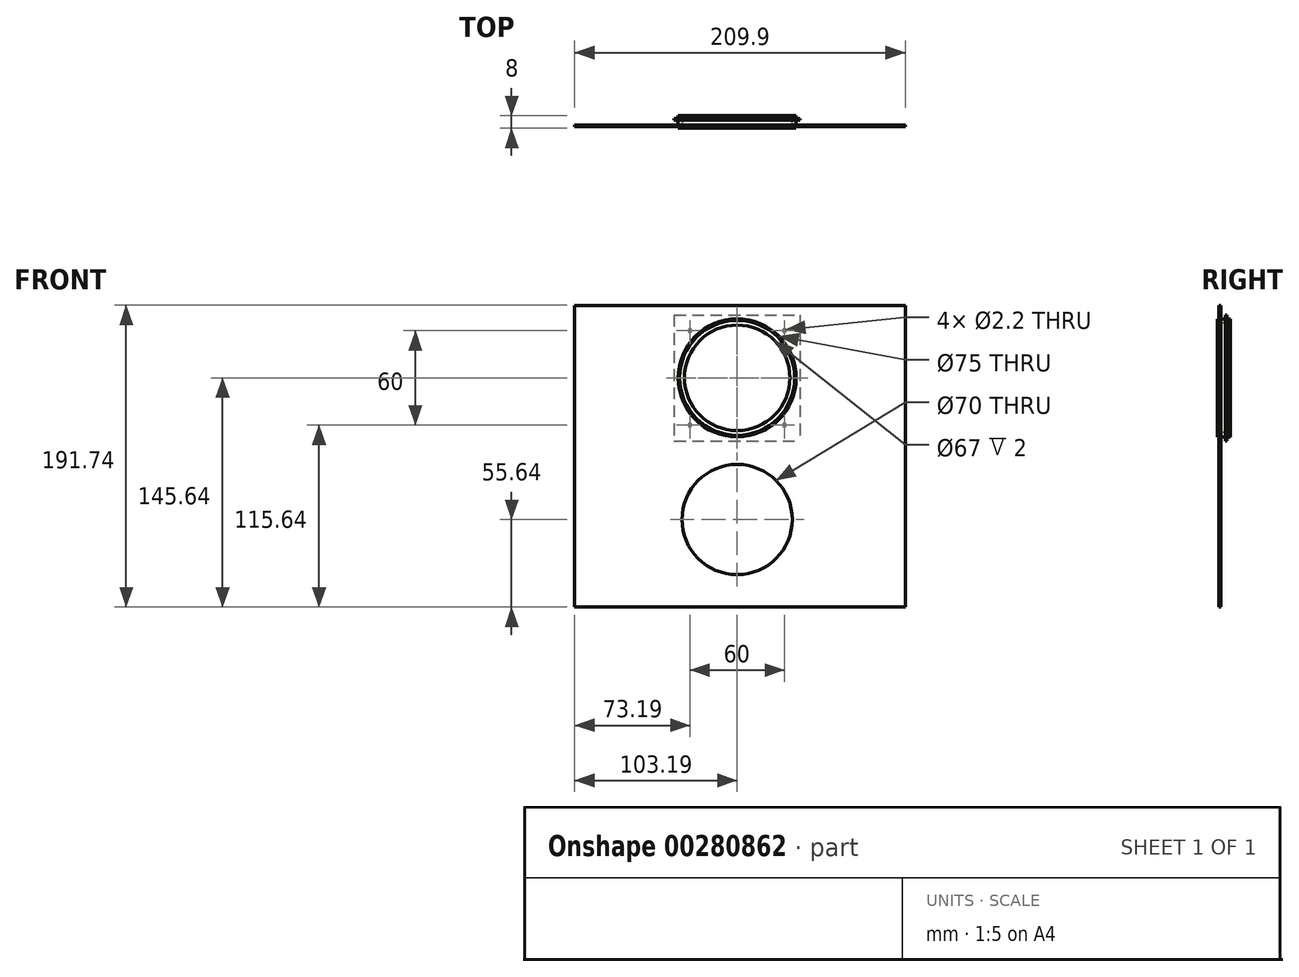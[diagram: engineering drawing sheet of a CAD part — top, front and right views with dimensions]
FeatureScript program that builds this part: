
annotation { "Feature Type Name" : "Feature", "Feature Type Description" : "" }
export const myFeature = defineFeature(function(context is Context, id is Id, definition is map)
    precondition{}
    {
        {
            var Q0;
            Q0=qCreatedBy(makeId("Front.planeOp"),FACE);
            cPlane(context, id + "F0", {"entities" : qUnion([Q0]), "cplaneType" : CPlaneType.OFFSET, "offset" : 5 * mm, "width" : 150 * mm, "height" : 150 * mm});
        }
        {
            var Q0;
            Q0=qCreatedBy(id+"F0.planeOp",FACE);
            var sketch = newSketch(context, id + "F1", { "sketchPlane" : qUnion([Q0])});
            skCircle(sketch, "E0", {"center": v(0, 0) * mm, "radius": 37.5 * mm});
            skCircle(sketch, "E1", {"center": v(0, -90) * mm, "radius": 35 * mm});
            skLineSegment(sketch, "E2.bottom", {"start": v(-103.2, 46.1) * mm, "end": v(106.7, 46.1) * mm});
            skLineSegment(sketch, "E2.top", {"start": v(-103.2, -145.64) * mm, "end": v(106.7, -145.64) * mm});
            skLineSegment(sketch, "E2.left", {"start": v(-103.2, 46.1) * mm, "end": v(-103.2, -145.64) * mm});
            skLineSegment(sketch, "E2.right", {"start": v(106.7, 46.1) * mm, "end": v(106.7, -145.64) * mm});
            skSolve(sketch);
        }
        {
            var Q0;
            Q0=qSketchRegion(id+"F1",true);
            extrude(context, id + "F2", {"entities" : qUnion([Q0]), "oppositeDirection" : true, "depth" : 1 * mm});
        }
        {
            var Q0;
            Q0=qCreatedBy(makeId("Right.planeOp"),FACE);
            var sketch = newSketch(context, id + "F3", { "sketchPlane" : qUnion([Q0])});
            skLineSegment(sketch, "E3", {"start": v(19.32, 0) * mm, "end": v(-16.11, 0) * mm, "construction": true});
            skLineSegment(sketch, "E4", {"start": v(-6, 37.5) * mm, "end": v(-6, 36.5) * mm});
            skLineSegment(sketch, "E5", {"start": v(-6, 36.5) * mm, "end": v(0, 33.5) * mm});
            skLineSegment(sketch, "E6", {"start": v(0, 33.5) * mm, "end": v(0, 37.5) * mm});
            skLineSegment(sketch, "E7", {"start": v(0, 37.5) * mm, "end": v(-6, 37.5) * mm});
            skSolve(sketch);
        }
        {
            var Q0;
            Q0=qSketchRegion(id+"F3",true);
            var Q1;
            Q1=sQuery(id+"F3.wireOp",EDGE,"E3");
            revolve(context, id + "F4", {"entities" : qUnion([Q0]), "axis" : qUnion([Q1]), "revolveType" : RevolveType.FULL});
        }
        {
            var Q0;
            Q0=qCreatedBy(makeId("Front.planeOp"),FACE);
            var sketch = newSketch(context, id + "F5", { "sketchPlane" : qUnion([Q0])});
            skCircle(sketch, "E8", {"center": v(0, 0) * mm, "radius": 37.5 * mm});
            skLineSegment(sketch, "E9.bottom", {"start": v(-40, 40) * mm, "end": v(40, 40) * mm});
            skLineSegment(sketch, "E9.top", {"start": v(-40, -40) * mm, "end": v(40, -40) * mm});
            skLineSegment(sketch, "E9.left", {"start": v(-40, 40) * mm, "end": v(-40, -40) * mm});
            skLineSegment(sketch, "E9.right", {"start": v(40, 40) * mm, "end": v(40, -40) * mm});
            skCircle(sketch, "E10", {"center": v(-30, 30) * mm, "radius": 1.1 * mm});
            skCircle(sketch, "E11", {"center": v(-30, -30) * mm, "radius": 1.1 * mm});
            skCircle(sketch, "E12", {"center": v(30, -30) * mm, "radius": 1.1 * mm});
            skCircle(sketch, "E13", {"center": v(30, 30) * mm, "radius": 1.1 * mm});
            skLineSegment(sketch, "E14.bottom", {"start": v(30, -30) * mm, "end": v(-30, -30) * mm, "construction": true});
            skLineSegment(sketch, "E14.top", {"start": v(30, 30) * mm, "end": v(-30, 30) * mm, "construction": true});
            skLineSegment(sketch, "E14.left", {"start": v(30, -30) * mm, "end": v(30, 30) * mm, "construction": true});
            skLineSegment(sketch, "E14.right", {"start": v(-30, -30) * mm, "end": v(-30, 30) * mm, "construction": true});
            skSolve(sketch);
        }
        {
            var Q0;
            Q0=qSketchRegion(id+"F5",true);
            extrude(context, id + "F6", {"entities" : qUnion([Q0]), "depth" : 1 * mm});
        }
        {
            var Q0;
            Q0=makeQuery(id+"F4.opRevolve","SWEPT_FACE",FACE,{"disambiguationData":[OSD([sQuery(id+"F3.wireOp",EDGE,"E6")])]});
            extrude(context, id + "F7", {"entities" : qUnion([Q0]), "operationType" : NewBodyOperationType.ADD, "depth" : 2 * mm});
        }
    });
